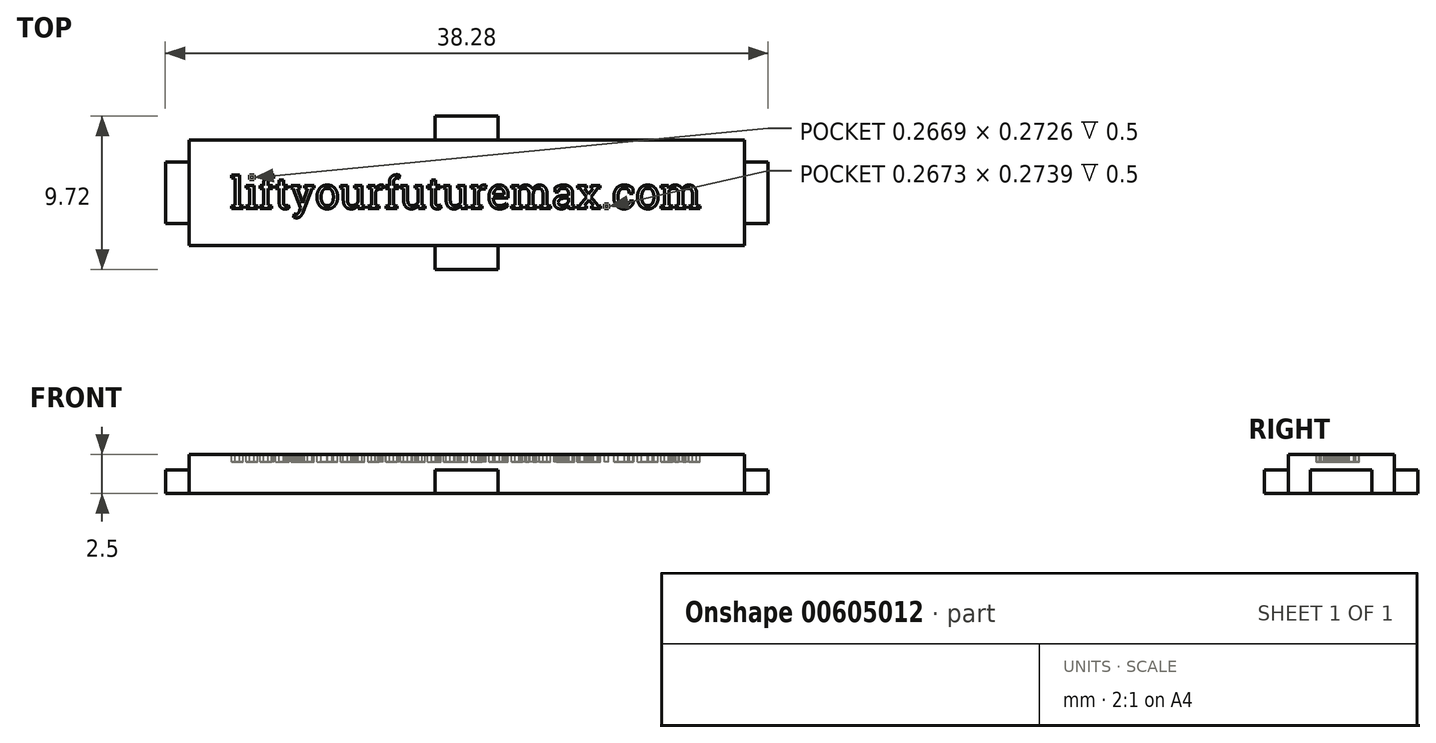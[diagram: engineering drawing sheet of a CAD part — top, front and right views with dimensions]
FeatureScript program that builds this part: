
annotation { "Feature Type Name" : "Feature", "Feature Type Description" : "" }
export const myFeature = defineFeature(function(context is Context, id is Id, definition is map)
    precondition{}
    {
        {
            var Q0;
            Q0=qCreatedBy(makeId("Top.planeOp"),FACE);
            var sketch = newSketch(context, id + "F0", { "sketchPlane" : qUnion([Q0])});
            skLineSegment(sketch, "E0.bottom", {"start": v(-19.14, 3.36) * mm, "end": v(19.14, 3.36) * mm});
            skLineSegment(sketch, "E0.top", {"start": v(-19.14, -3.36) * mm, "end": v(19.14, -3.36) * mm});
            skLineSegment(sketch, "E0.left", {"start": v(-19.14, 3.36) * mm, "end": v(-19.14, -3.36) * mm});
            skLineSegment(sketch, "E0.right", {"start": v(19.14, 3.36) * mm, "end": v(19.14, -3.36) * mm});
            skSolve(sketch);
        }
        {
            var Q0;
            Q0 = qSketchRegion(id + "F0", true);
            extrude(context, id + "F1", {"entities" : qUnion([Q0]), "depth" : 2.5 * mm, "offsetDistance" : 25 * mm});
        }
        {
            var Q0;
            Q0=makeQuery(id+"F1.opExtrude","SWEPT_FACE",FACE,{"disambiguationData":[OSD([sQuery(id+"F0.wireOp",EDGE,"E0.top")])]});
            var sketch = newSketch(context, id + "F2", { "sketchPlane" : qUnion([Q0])});
            skLineSegment(sketch, "E1.bottom", {"start": v(-19.14, 2.5) * mm, "end": v(-17.64, 2.5) * mm});
            skLineSegment(sketch, "E1.top", {"start": v(-19.14, 1.5) * mm, "end": v(-17.64, 1.5) * mm});
            skLineSegment(sketch, "E1.left", {"start": v(-19.14, 2.5) * mm, "end": v(-19.14, 1.5) * mm});
            skLineSegment(sketch, "E1.right", {"start": v(-17.64, 2.5) * mm, "end": v(-17.64, 1.5) * mm});
            skLineSegment(sketch, "E2.bottom", {"start": v(19.14, 2.5) * mm, "end": v(17.64, 2.5) * mm});
            skLineSegment(sketch, "E2.top", {"start": v(19.14, 1.5) * mm, "end": v(17.64, 1.5) * mm});
            skLineSegment(sketch, "E2.left", {"start": v(19.14, 2.5) * mm, "end": v(19.14, 1.5) * mm});
            skLineSegment(sketch, "E2.right", {"start": v(17.64, 2.5) * mm, "end": v(17.64, 1.5) * mm});
            skSolve(sketch);
        }
        {
            var Q0;
            Q0 = qSketchRegion(id + "F2", true);
            extrude(context, id + "F3", {"entities" : qUnion([Q0]), "operationType" : NewBodyOperationType.REMOVE, "oppositeDirection" : true, "depth" : 25 * mm, "offsetDistance" : 25 * mm});
        }
        {
            var Q0;
            Q0=makeQuery(id+"F3.boolean.opBoolean","COPY",FACE,{"derivedFrom":makeQuery(id+"F3.opExtrude","SWEPT_FACE",FACE,{"disambiguationData":[OSD([sQuery(id+"F2.wireOp",EDGE,"E1.top")])]})});
            var sketch = newSketch(context, id + "F4", { "sketchPlane" : qUnion([Q0])});
            skLineSegment(sketch, "E3.bottom", {"start": v(-19.14, 3.36) * mm, "end": v(-17.64, 3.36) * mm});
            skLineSegment(sketch, "E3.top", {"start": v(-19.14, 1.96) * mm, "end": v(-17.64, 1.96) * mm});
            skLineSegment(sketch, "E3.left", {"start": v(-19.14, 3.36) * mm, "end": v(-19.14, 1.96) * mm});
            skLineSegment(sketch, "E3.right", {"start": v(-17.64, 3.36) * mm, "end": v(-17.64, 1.96) * mm});
            skLineSegment(sketch, "E4.MirrorCS", {"start": v(-19.14, -1.96) * mm, "end": v(-17.64, -1.96) * mm});
            skLineSegment(sketch, "E5.MirrorCS", {"start": v(-19.14, -3.36) * mm, "end": v(-17.64, -3.36) * mm});
            skLineSegment(sketch, "E6.MirrorCS", {"start": v(-17.64, -3.36) * mm, "end": v(-17.64, -1.96) * mm});
            skLineSegment(sketch, "E7.MirrorCS", {"start": v(-19.14, -3.36) * mm, "end": v(-19.14, -1.96) * mm});
            skLineSegment(sketch, "E8.MirrorCS", {"start": v(19.14, 3.36) * mm, "end": v(19.14, 1.96) * mm});
            skLineSegment(sketch, "E9.MirrorCS", {"start": v(19.14, 3.36) * mm, "end": v(17.64, 3.36) * mm});
            skLineSegment(sketch, "E10.MirrorCS", {"start": v(17.64, 3.36) * mm, "end": v(17.64, 1.96) * mm});
            skLineSegment(sketch, "E11.MirrorCS", {"start": v(19.14, 1.96) * mm, "end": v(17.64, 1.96) * mm});
            skLineSegment(sketch, "E12.MirrorCS", {"start": v(19.14, -1.96) * mm, "end": v(17.64, -1.96) * mm});
            skLineSegment(sketch, "E13.MirrorCS", {"start": v(17.64, -3.36) * mm, "end": v(17.64, -1.96) * mm});
            skLineSegment(sketch, "E14.MirrorCS", {"start": v(19.14, -3.36) * mm, "end": v(17.64, -3.36) * mm});
            skLineSegment(sketch, "E15.MirrorCS", {"start": v(19.14, -3.36) * mm, "end": v(19.14, -1.96) * mm});
            skSolve(sketch);
        }
        {
            var Q0;
            Q0 = qSketchRegion(id + "F4", true);
            extrude(context, id + "F5", {"entities" : qUnion([Q0]), "operationType" : NewBodyOperationType.REMOVE, "oppositeDirection" : true, "depth" : 25 * mm, "offsetDistance" : 25 * mm});
        }
        {
            var Q0;
            Q0=makeQuery(id+"F1.opExtrude","SWEPT_FACE",FACE,{"disambiguationData":[OSD([sQuery(id+"F0.wireOp",EDGE,"E0.bottom")])]});
            var sketch = newSketch(context, id + "F6", { "sketchPlane" : qUnion([Q0])});
            skLineSegment(sketch, "E16.bottom", {"start": v(-2, 0) * mm, "end": v(2, 0) * mm});
            skLineSegment(sketch, "E16.top", {"start": v(-2, 1.5) * mm, "end": v(2, 1.5) * mm});
            skLineSegment(sketch, "E16.left", {"start": v(-2, 0) * mm, "end": v(-2, 1.5) * mm});
            skLineSegment(sketch, "E16.right", {"start": v(2, 0) * mm, "end": v(2, 1.5) * mm});
            skSolve(sketch);
        }
        {
            var Q0;
            Q0 = qSketchRegion(id + "F6", true);
            extrude(context, id + "F7", {"entities" : qUnion([Q0]), "operationType" : NewBodyOperationType.ADD, "depth" : 1.5 * mm, "offsetDistance" : 25 * mm});
        }
        {
            var Q0;
            Q0=makeQuery(id+"F1.opExtrude","SWEPT_FACE",FACE,{"disambiguationData":[OSD([sQuery(id+"F0.wireOp",EDGE,"E0.top")])]});
            var sketch = newSketch(context, id + "F8", { "sketchPlane" : qUnion([Q0])});
            skLineSegment(sketch, "E17.bottom", {"start": v(-2, 0) * mm, "end": v(2, 0) * mm});
            skLineSegment(sketch, "E17.top", {"start": v(-2, 1.5) * mm, "end": v(2, 1.5) * mm});
            skLineSegment(sketch, "E17.left", {"start": v(-2, 0) * mm, "end": v(-2, 1.5) * mm});
            skLineSegment(sketch, "E17.right", {"start": v(2, 0) * mm, "end": v(2, 1.5) * mm});
            skSolve(sketch);
        }
        {
            var Q0;
            Q0 = qSketchRegion(id + "F8", true);
            extrude(context, id + "F9", {"entities" : qUnion([Q0]), "operationType" : NewBodyOperationType.ADD, "depth" : 1.5 * mm, "offsetDistance" : 25 * mm});
        }
        {
            var Q0;
            Q0=makeQuery(id+"F1.opExtrude","CAP_FACE",FACE,{"disambiguationData":[OSD([sQuery(id+"F0.wireOp",EDGE,"E0.bottom"),sQuery(id+"F0.wireOp",EDGE,"E0.top"),sQuery(id+"F0.wireOp",EDGE,"E0.left"),sQuery(id+"F0.wireOp",EDGE,"E0.right")])],"isStart":false});
            var sketch = newSketch(context, id + "F10", { "sketchPlane" : qUnion([Q0])});
            skText(sketch, "E18", { "text": "liftyourfuturemax.com", "fontName": "RobotoSlab-Regular.ttf"});
            const initialGuessF10  = {"E18": [-0.015, -0.001, 1, 0, 0.002]};
            skSetInitialGuess(sketch, initialGuessF10);
            skSolve(sketch);
        }
        {
            var Q0;
            Q0 = qSketchRegion(id + "F10", true);
            extrude(context, id + "F11", {"entities" : qUnion([Q0]), "operationType" : NewBodyOperationType.REMOVE, "oppositeDirection" : true, "depth" : 0.5 * mm, "offsetDistance" : 25 * mm});
        }
    });
